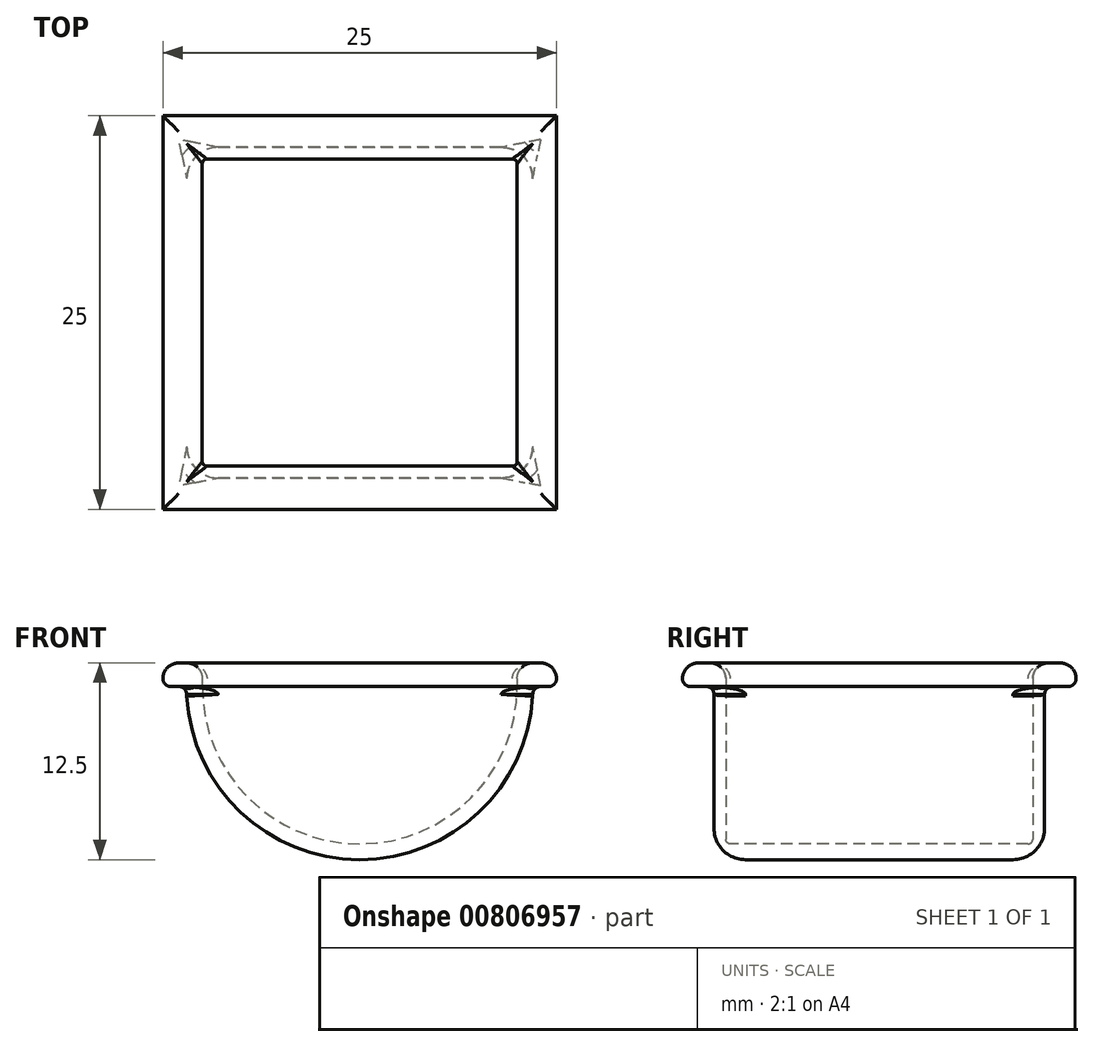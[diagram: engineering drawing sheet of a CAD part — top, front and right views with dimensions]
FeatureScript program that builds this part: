
annotation { "Feature Type Name" : "Feature", "Feature Type Description" : "" }
export const myFeature = defineFeature(function(context is Context, id is Id, definition is map)
    precondition{}
    {
        {
            var Q0;
            Q0=qCreatedBy(makeId("Front.planeOp"),FACE);
            var sketch = newSketch(context, id + "F0", { "sketchPlane" : qUnion([Q0])});
            skCircle(sketch, "E0", {"center": v(0, 0) * mm, "radius": 11 * mm});
            skSolve(sketch);
        }
        {
            var Q0;
            Q0 = qSketchRegion(id + "F0", true);
            extrude(context, id + "F1", {"entities" : qUnion([Q0]), "depth" : 10.5 * mm, "offsetDistance" : 25 * mm, "hasSecondDirection" : true, "secondDirectionOppositeDirection" : true, "secondDirectionDepth" : 10.5 * mm});
        }
        {
            var Q0;
            Q0=qCreatedBy(makeId("Top.planeOp"),FACE);
            var sketch = newSketch(context, id + "F2", { "sketchPlane" : qUnion([Q0])});
            skLineSegment(sketch, "E1.bottom", {"start": v(11, -11) * mm, "end": v(-11, -11) * mm});
            skLineSegment(sketch, "E1.top", {"start": v(11, 11) * mm, "end": v(-11, 11) * mm});
            skLineSegment(sketch, "E1.left", {"start": v(11, -11) * mm, "end": v(11, 11) * mm});
            skLineSegment(sketch, "E1.right", {"start": v(-11, -11) * mm, "end": v(-11, 11) * mm});
            skPoint(sketch, "E1.middle", {"position": v(0, 0) * mm});
            skSolve(sketch);
        }
        {
            var Q0;
            Q0 = qSketchRegion(id + "F2", true);
            extrude(context, id + "F3", {"entities" : qUnion([Q0]), "operationType" : NewBodyOperationType.REMOVE, "depth" : 25 * mm, "offsetDistance" : 25 * mm});
        }
        {
            var Q0;
            Q0=qCreatedBy(makeId("Front.planeOp"),FACE);
            var sketch = newSketch(context, id + "F4", { "sketchPlane" : qUnion([Q0])});
            skCircle(sketch, "E2", {"center": v(0, 0) * mm, "radius": 10 * mm});
            skSolve(sketch);
        }
        {
            var Q0;
            Q0 = qSketchRegion(id + "F4", true);
            extrude(context, id + "F5", {"entities" : qUnion([Q0]), "operationType" : NewBodyOperationType.REMOVE, "oppositeDirection" : true, "depth" : 9.75 * mm, "offsetDistance" : 25 * mm, "hasSecondDirection" : true, "secondDirectionOppositeDirection" : false, "secondDirectionDepth" : 9.75 * mm});
        }
        {
            var Q0;
            Q0=makeQuery(id+"F3.boolean.opBoolean","COPY",FACE,{"derivedFrom":makeQuery(id+"F3.opExtrude","CAP_FACE",FACE,{"disambiguationData":[OSD([sQuery(id+"F2.wireOp",EDGE,"E1.bottom"),sQuery(id+"F2.wireOp",EDGE,"E1.top"),sQuery(id+"F2.wireOp",EDGE,"E1.left"),sQuery(id+"F2.wireOp",EDGE,"E1.right")])],"isStart":true})});
            var sketch = newSketch(context, id + "F6", { "sketchPlane" : qUnion([Q0])});
            skLineSegment(sketch, "E3.bottom", {"start": v(10, -9.75) * mm, "end": v(-10, -9.75) * mm});
            skLineSegment(sketch, "E3.top", {"start": v(10, 9.75) * mm, "end": v(-10, 9.75) * mm});
            skLineSegment(sketch, "E3.left", {"start": v(10, -9.75) * mm, "end": v(10, 9.75) * mm});
            skLineSegment(sketch, "E3.right", {"start": v(-10, -9.75) * mm, "end": v(-10, 9.75) * mm});
            skPoint(sketch, "E3.middle", {"position": v(0, 0) * mm});
            skLineSegment(sketch, "E4.bottom", {"start": v(12.5, -12.5) * mm, "end": v(-12.5, -12.5) * mm});
            skLineSegment(sketch, "E4.top", {"start": v(12.5, 12.5) * mm, "end": v(-12.5, 12.5) * mm});
            skLineSegment(sketch, "E4.left", {"start": v(12.5, -12.5) * mm, "end": v(12.5, 12.5) * mm});
            skLineSegment(sketch, "E4.right", {"start": v(-12.5, -12.5) * mm, "end": v(-12.5, 12.5) * mm});
            skSolve(sketch);
        }
        {
            var Q0;
            Q0 = qSketchRegion(id + "F6", true);
            extrude(context, id + "F7", {"entities" : qUnion([Q0]), "operationType" : NewBodyOperationType.ADD, "depth" : 1.5 * mm, "offsetDistance" : 25 * mm});
        }
        {
            var Q0;
            Q0=makeQuery(id+"F7.opExtrude","CAP_FACE",FACE,{"disambiguationData":[OSD([sQuery(id+"F6.wireOp",EDGE,"E3.bottom"),sQuery(id+"F6.wireOp",EDGE,"E3.top"),sQuery(id+"F6.wireOp",EDGE,"E3.left"),sQuery(id+"F6.wireOp",EDGE,"E3.right"),sQuery(id+"F6.wireOp",EDGE,"E4.bottom"),sQuery(id+"F6.wireOp",EDGE,"E4.top"),sQuery(id+"F6.wireOp",EDGE,"E4.left"),sQuery(id+"F6.wireOp",EDGE,"E4.right")])],"isStart":false});
            fillet(context, id + "F8", {"entities" : qUnion([Q0]), "radius" : 1 * mm, "tangentPropagation" : true, "allowEdgeOverflow" : false});
        }
        {
            var Q0;
            Q0=makeQuery(id+"F7.opExtrude","CAP_FACE",FACE,{"disambiguationData":[OSD([sQuery(id+"F6.wireOp",EDGE,"E3.bottom"),sQuery(id+"F6.wireOp",EDGE,"E3.top"),sQuery(id+"F6.wireOp",EDGE,"E3.left"),sQuery(id+"F6.wireOp",EDGE,"E3.right"),sQuery(id+"F6.wireOp",EDGE,"E4.bottom"),sQuery(id+"F6.wireOp",EDGE,"E4.top"),sQuery(id+"F6.wireOp",EDGE,"E4.left"),sQuery(id+"F6.wireOp",EDGE,"E4.right")])],"isStart":true});
            fillet(context, id + "F9", {"entities" : qUnion([Q0]), "radius" : .5 * mm, "tangentPropagation" : true, "allowEdgeOverflow" : false});
        }
        {
            var Q0;
            Q0=makeQuery(id+"F1.opExtrude","CAP_EDGE",EDGE,{"disambiguationData":[OSD([sQuery(id+"F0.wireOp",EDGE,"E0")])],"isStart":false});
            var Q1;
            Q1=makeQuery(id+"F1.opExtrude","CAP_EDGE",EDGE,{"disambiguationData":[OSD([sQuery(id+"F0.wireOp",EDGE,"E0")])],"isStart":true});
            fillet(context, id + "F10", {"entities" : qUnion([Q0, Q1]), "radius" : 2 * mm, "tangentPropagation" : true, "allowEdgeOverflow" : false});
        }
        {
            var Q0;
            Q0=makeQuery(id+"F5.boolean.opBoolean","COPY",EDGE,{"derivedFrom":makeQuery(id+"F5.opExtrude","CAP_EDGE",EDGE,{"disambiguationData":[OSD([sQuery(id+"F4.wireOp",EDGE,"E2")])],"isStart":false})});
            var Q1;
            Q1=makeQuery(id+"F5.boolean.opBoolean","COPY",EDGE,{"derivedFrom":makeQuery(id+"F5.opExtrude","CAP_EDGE",EDGE,{"disambiguationData":[OSD([sQuery(id+"F4.wireOp",EDGE,"E2")])],"isStart":true})});
            fillet(context, id + "F11", {"entities" : qUnion([Q0, Q1]), "radius" : .3 * mm, "tangentPropagation" : true, "allowEdgeOverflow" : false});
        }
    });
